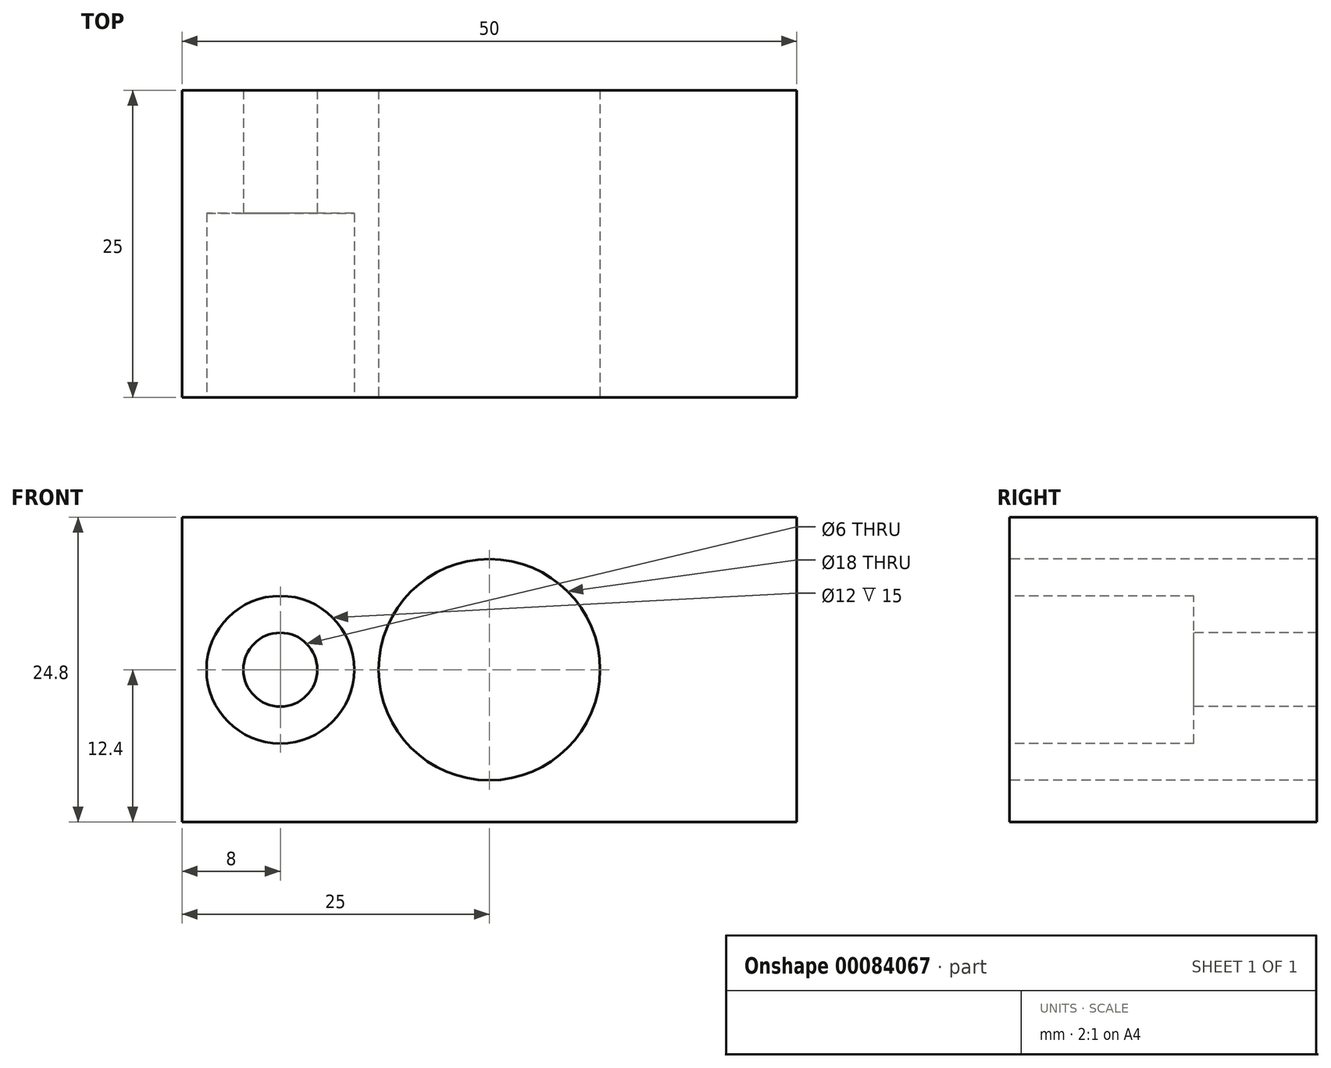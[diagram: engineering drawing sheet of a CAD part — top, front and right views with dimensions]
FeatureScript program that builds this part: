
annotation { "Feature Type Name" : "Feature", "Feature Type Description" : "" }
export const myFeature = defineFeature(function(context is Context, id is Id, definition is map)
    precondition{}
    {
        {
            var Q0;
            Q0=qCreatedBy(makeId("Front.planeOp"),FACE);
            var sketch = newSketch(context, id + "F0", { "sketchPlane" : qUnion([Q0])});
            skLineSegment(sketch, "E0.bottom", {"start": v(0, 0) * mm, "end": v(50, 0) * mm});
            skLineSegment(sketch, "E0.top", {"start": v(0, 24.8) * mm, "end": v(50, 24.8) * mm});
            skLineSegment(sketch, "E0.left", {"start": v(0, 0) * mm, "end": v(0, 24.8) * mm});
            skLineSegment(sketch, "E0.right", {"start": v(50, 0) * mm, "end": v(50, 24.8) * mm});
            skCircle(sketch, "E1", {"center": v(25, 12.4) * mm, "radius": 9 * mm});
            skCircle(sketch, "E2", {"center": v(8, 12.4) * mm, "radius": 3 * mm});
            skCircle(sketch, "E3", {"center": v(8, 12.4) * mm, "radius": 6 * mm});
            skSolve(sketch);
        }
        {
            var Q0;
            Q0=makeQuery(id+"F0.imprint","IMPRINT",FACE,{"disambiguationData":[TD([[makeQuery(id+"F0.imprint","IMPRINT",EDGE,{"derivedFrom":sQuery(id+"F0.wireOp",EDGE,"E0.bottom")}),1.0]])]});
            var Q1;
            Q1=makeQuery(id+"F0.imprint","IMPRINT",FACE,{"disambiguationData":[TD([[makeQuery(id+"F0.imprint","IMPRINT",EDGE,{"derivedFrom":sQuery(id+"F0.wireOp",EDGE,"E2")}),-1.0]])]});
            extrude(context, id + "F1", {"entities" : qUnion([Q0, Q1]), "oppositeDirection" : true, "depth" : 25 * mm});
        }
        {
            var Q0;
            Q0=makeQuery(id+"F0.imprint","IMPRINT",FACE,{"disambiguationData":[TD([[makeQuery(id+"F0.imprint","IMPRINT",EDGE,{"derivedFrom":sQuery(id+"F0.wireOp",EDGE,"E2")}),-1.0]])]});
            extrude(context, id + "F2", {"entities" : qUnion([Q0]), "operationType" : NewBodyOperationType.REMOVE, "oppositeDirection" : true, "depth" : 15 * mm});
        }
        {
            var Q0;
            Q0=qCreatedBy(makeId("Top.planeOp"),FACE);
            cPlane(context, id + "F3", {"entities" : qUnion([Q0]), "cplaneType" : CPlaneType.OFFSET, "offset" : 12.4 * mm, "width" : 150 * mm, "height" : 150 * mm});
        }
    });
